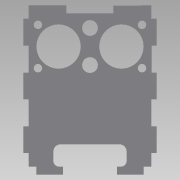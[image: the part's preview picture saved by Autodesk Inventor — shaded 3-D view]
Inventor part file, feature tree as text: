
AUTODESK INVENTOR PART (.ipt)
format: ipt  version: 2015 SP1 (Build 190203100, 203)  size: 249,856 bytes
history: native  units: mm
features: extrude x3, sketch x2
ambient origin geometry x8: Origin, YZ Plane, XZ Plane, XY Plane, X Axis, Y Axis, Z Axis, Center Point
bodies: Solid1 (feature_tree)
feature tree (5):
  sketch  "Sketch1"  dims[d2=20.0mm d4=15.0mm d5=20.0mm d7=15.0mm d10=180.0deg]
  extrude  "Extrusion1"  TaperAngle=180.0deg  [1 undecoded]
  extrude  "Extrusion2"  Depth=3.0mm
  extrude  "Extrusion3"  Depth=20.0mm
  sketch  "Sketch2"  dims[d11=2.0mm d12=3.0mm d14=20.0mm d16=20.0mm d17=20.0mm d19=20.0mm d46=7.675mm d47=7.675mm d48=3.0mm d49=0.0mm d50=0.5mm d51=1.0mm d52=180.0deg d53=10.0mm d54=10.0mm d55=90.0deg d56=1.0mm d57=0.5mm d58=1.0mm d59=5.0mm d60=10.0mm d61=1.0mm d62=1.0mm d63=1.0mm d64=0.0mm d65=3.0mm d66=0.0mm d67=8.061mm d68=8.061mm d69=1.0mm d70=1.0mm d71=3.0mm d72=0.0mm]
note: 1 required parameter value undecoded (feature->parameter linkage not recoverable at this tier; creation-order binding heuristic only, values carry confidence <= 0.55)
